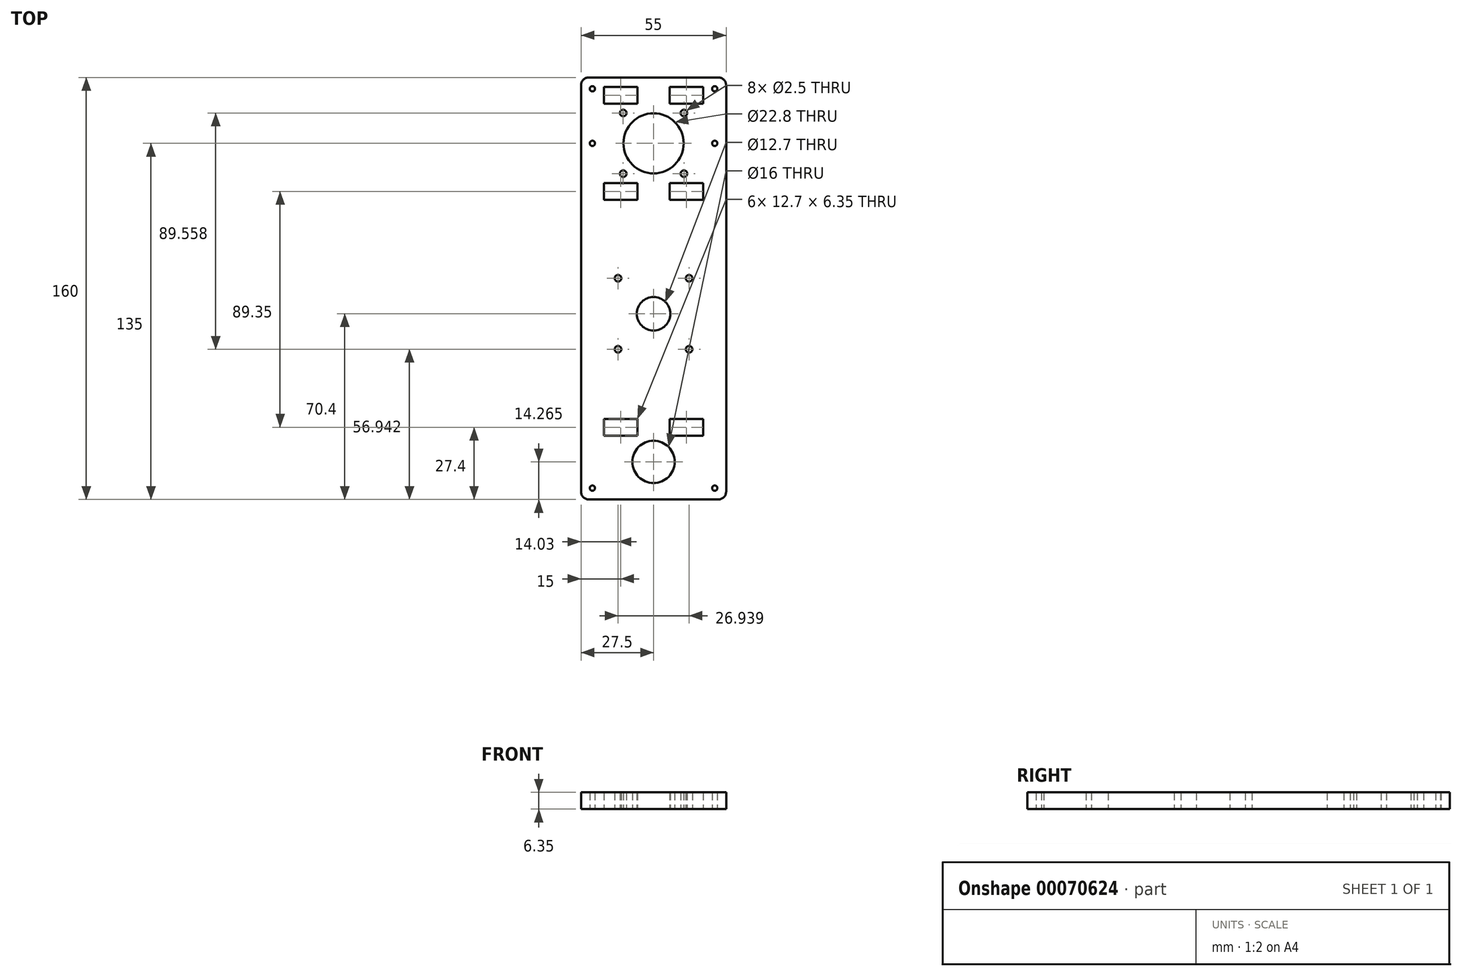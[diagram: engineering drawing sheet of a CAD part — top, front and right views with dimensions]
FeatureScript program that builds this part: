
annotation { "Feature Type Name" : "Feature", "Feature Type Description" : "" }
export const myFeature = defineFeature(function(context is Context, id is Id, definition is map)
    precondition{}
    {
        {
            var Q0;
            Q0=qCreatedBy(makeId("Top.planeOp"),FACE);
            var sketch = newSketch(context, id + "F0", { "sketchPlane" : qUnion([Q0])});
            skCircle(sketch, "E0", {"center": v(0, 0) * mm, "radius": 11.4 * mm});
            skLineSegment(sketch, "E1", {"start": v(0, 0) * mm, "end": v(0, 12.13) * mm});
            skLineSegment(sketch, "E2.bottom", {"start": v(-27.5, 25) * mm, "end": v(27.5, 25) * mm});
            skLineSegment(sketch, "E2.top", {"start": v(-27.5, -135) * mm, "end": v(27.5, -135) * mm});
            skLineSegment(sketch, "E2.left", {"start": v(-27.5, 25) * mm, "end": v(-27.5, -135) * mm});
            skLineSegment(sketch, "E2.right", {"start": v(27.5, 25) * mm, "end": v(27.5, -135) * mm});
            skPoint(sketch, "E3", {"position": v(-11.5, 11.5) * mm});
            skPoint(sketch, "E4.0.1.0", {"position": v(-11.5, -11.5) * mm});
            skPoint(sketch, "E4.1.0.0", {"position": v(11.5, 11.5) * mm});
            skPoint(sketch, "E4.1.1.0", {"position": v(11.5, -11.5) * mm});
            skLineSegment(sketch, "E4.direction1", {"start": v(-11.5, 11.5) * mm, "end": v(11.5, 11.5) * mm, "construction": true});
            skLineSegment(sketch, "E4.direction2", {"start": v(-11.5, 11.5) * mm, "end": v(-11.5, -11.5) * mm, "construction": true});
            skLineSegment(sketch, "E5.bottom", {"start": v(-18.85, 21.43) * mm, "end": v(-6.15, 21.43) * mm});
            skLineSegment(sketch, "E5.top", {"start": v(-18.85, 15.08) * mm, "end": v(-6.15, 15.08) * mm});
            skLineSegment(sketch, "E5.left", {"start": v(-18.85, 21.43) * mm, "end": v(-18.85, 15.07) * mm});
            skLineSegment(sketch, "E5.right", {"start": v(-6.15, 21.43) * mm, "end": v(-6.15, 15.07) * mm});
            skPoint(sketch, "E6", {"position": v(-12.5, 21.43) * mm});
            skLineSegment(sketch, "E7.0.1.0", {"start": v(-18.85, -21.43) * mm, "end": v(-6.15, -21.43) * mm});
            skLineSegment(sketch, "E7.0.1.1", {"start": v(-18.85, -15.07) * mm, "end": v(-6.15, -15.07) * mm});
            skLineSegment(sketch, "E7.0.1.2", {"start": v(-18.85, -15.07) * mm, "end": v(-18.85, -21.43) * mm});
            skLineSegment(sketch, "E7.0.1.3", {"start": v(-6.15, -15.07) * mm, "end": v(-6.15, -21.43) * mm});
            skPoint(sketch, "E7.0.1.4", {"position": v(-12.5, -15.07) * mm});
            skLineSegment(sketch, "E7.1.0.0", {"start": v(6.15, 15.08) * mm, "end": v(18.85, 15.08) * mm});
            skLineSegment(sketch, "E7.1.0.1", {"start": v(6.15, 21.43) * mm, "end": v(18.85, 21.43) * mm});
            skLineSegment(sketch, "E7.1.0.2", {"start": v(6.15, 21.43) * mm, "end": v(6.15, 15.07) * mm});
            skLineSegment(sketch, "E7.1.0.3", {"start": v(18.85, 21.43) * mm, "end": v(18.85, 15.07) * mm});
            skPoint(sketch, "E7.1.0.4", {"position": v(12.5, 21.43) * mm});
            skLineSegment(sketch, "E7.1.1.0", {"start": v(6.15, -21.43) * mm, "end": v(18.85, -21.43) * mm});
            skLineSegment(sketch, "E7.1.1.1", {"start": v(6.15, -15.07) * mm, "end": v(18.85, -15.07) * mm});
            skLineSegment(sketch, "E7.1.1.2", {"start": v(6.15, -15.07) * mm, "end": v(6.15, -21.43) * mm});
            skLineSegment(sketch, "E7.1.1.3", {"start": v(18.85, -15.07) * mm, "end": v(18.85, -21.43) * mm});
            skPoint(sketch, "E7.1.1.4", {"position": v(12.5, -15.07) * mm});
            skLineSegment(sketch, "E7.direction1", {"start": v(-18.85, 15.07) * mm, "end": v(6.15, 15.07) * mm, "construction": true});
            skLineSegment(sketch, "E7.direction2", {"start": v(-18.85, 15.07) * mm, "end": v(-18.85, -21.43) * mm, "construction": true});
            skPoint(sketch, "E8", {"position": v(0, -120.73) * mm});
            skPoint(sketch, "E9", {"position": v(-23.17, -130.67) * mm});
            skPoint(sketch, "E10", {"position": v(-23.17, 20.68) * mm});
            skPoint(sketch, "E11", {"position": v(-23.17, 0) * mm});
            skPoint(sketch, "E12.MirrorP", {"position": v(23.17, 20.68) * mm});
            skPoint(sketch, "E13.MirrorP", {"position": v(23.17, 0) * mm});
            skPoint(sketch, "E14.MirrorP", {"position": v(23.17, -130.67) * mm});
            skPoint(sketch, "E15", {"position": v(18.85, -18.25) * mm});
            skPoint(sketch, "E16", {"position": v(0, -64.6) * mm});
            skCircle(sketch, "E17", {"center": v(0, -64.6) * mm, "radius": 6.35 * mm});
            skPoint(sketch, "E18.3.0", {"position": v(-13.47, -51.13) * mm});
            skLineSegment(sketch, "E19", {"start": v(-13.42, -25) * mm, "end": v(-13.42, -25) * mm});
            skPoint(sketch, "E20.MirrorP", {"position": v(13.47, -51.13) * mm});
            skPoint(sketch, "E21.3.0", {"position": v(-13.47, -78.06) * mm});
            skPoint(sketch, "E22.MirrorP", {"position": v(13.47, -78.06) * mm});
            skLineSegment(sketch, "E23", {"start": v(0, -64.6) * mm, "end": v(56.6, -64.6) * mm, "construction": true});
            skCircle(sketch, "E24", {"center": v(0, -120.73) * mm, "radius": 8 * mm});
            skLineSegment(sketch, "E25.0.1.4", {"start": v(6.15, -104.42) * mm, "end": v(6.15, -110.77) * mm});
            skLineSegment(sketch, "E25.0.1.5", {"start": v(6.15, -104.42) * mm, "end": v(18.85, -104.42) * mm});
            skLineSegment(sketch, "E25.0.1.6", {"start": v(18.85, -104.42) * mm, "end": v(18.85, -110.77) * mm});
            skLineSegment(sketch, "E25.0.1.7", {"start": v(6.15, -110.77) * mm, "end": v(18.85, -110.77) * mm});
            skLineSegment(sketch, "E25.direction1", {"start": v(-18.85, -21.43) * mm, "end": v(-43.85, -21.43) * mm, "construction": true});
            skLineSegment(sketch, "E26.MirrorCS", {"start": v(-6.15, -104.42) * mm, "end": v(-6.15, -110.77) * mm});
            skLineSegment(sketch, "E27.MirrorCS", {"start": v(-18.85, -104.42) * mm, "end": v(-18.85, -110.77) * mm});
            skLineSegment(sketch, "E28.MirrorCS", {"start": v(-6.15, -110.77) * mm, "end": v(-18.85, -110.77) * mm});
            skLineSegment(sketch, "E29.MirrorCS", {"start": v(-6.15, -104.42) * mm, "end": v(-18.85, -104.42) * mm});
            skSolve(sketch);
        }
        {
            var Q0;
            Q0=makeQuery(id+"F0.imprint","IMPRINT",FACE,{"disambiguationData":[TD([[makeQuery(id+"F0.imprint","IMPRINT",EDGE,{"derivedFrom":sQuery(id+"F0.wireOp",EDGE,"E0")}),-1.0]])]});
            extrude(context, id + "F1", {"entities" : qUnion([Q0]), "depth" : 6.35 * mm});
        }
        {
            var Q0;
            Q0=sQuery(id+"F0.wireOp",VERTEX,"E3");
            var Q1;
            Q1=sQuery(id+"F0.wireOp",VERTEX,"E4.1.0.0");
            var Q2;
            Q2=sQuery(id+"F0.wireOp",VERTEX,"E4.1.1.0");
            var Q3;
            Q3=sQuery(id+"F0.wireOp",VERTEX,"E4.0.1.0");
            var Q4;
            Q4=sQuery(id+"F0.wireOp",VERTEX,"E18.3.0");
            var Q5;
            Q5=sQuery(id+"F0.wireOp",VERTEX,"E20.MirrorP");
            var Q6;
            Q6=sQuery(id+"F0.wireOp",VERTEX,"E22.MirrorP");
            var Q7;
            Q7=sQuery(id+"F0.wireOp",VERTEX,"E21.3.0");
            var Q8;
            Q8=makeQuery(id+"F1.opExtrude","SWEPT_BODY",BODY,{"disambiguationData":[OSD([sQuery(id+"F0.wireOp",EDGE,"E0"),sQuery(id+"F0.wireOp",EDGE,"E2.bottom"),sQuery(id+"F0.wireOp",EDGE,"E2.top"),sQuery(id+"F0.wireOp",EDGE,"E2.left"),sQuery(id+"F0.wireOp",EDGE,"E2.right")])]});
            hole(context, id + "F2", {"style" : HoleStyle.SIMPLE, "endStyle" : HoleEndStyle.THROUGH, "oppositeDirection" : true, "holeDiameter" : 2.5 * mm, "locations" : qUnion([Q0, Q1, Q2, Q3, Q4, Q5, Q6, Q7]), "scope" : qUnion([Q8]), "isTappedThrough" : true});
        }
        {
            var Q0;
            Q0=makeQuery(id+"F1.opExtrude","SWEPT_EDGE",EDGE,{"disambiguationData":[OSD([sQuery(id+"F0.wireOp",EDGE,"E2.top"),sQuery(id+"F0.wireOp",EDGE,"E2.left")])]});
            var Q1;
            Q1=makeQuery(id+"F1.opExtrude","SWEPT_EDGE",EDGE,{"disambiguationData":[OSD([sQuery(id+"F0.wireOp",EDGE,"E2.top"),sQuery(id+"F0.wireOp",EDGE,"E2.right")])]});
            var Q2;
            Q2=makeQuery(id+"F1.opExtrude","SWEPT_EDGE",EDGE,{"disambiguationData":[OSD([sQuery(id+"F0.wireOp",EDGE,"E2.bottom"),sQuery(id+"F0.wireOp",EDGE,"E2.right")])]});
            var Q3;
            Q3=makeQuery(id+"F1.opExtrude","SWEPT_EDGE",EDGE,{"disambiguationData":[OSD([sQuery(id+"F0.wireOp",EDGE,"E2.bottom"),sQuery(id+"F0.wireOp",EDGE,"E2.left")])]});
            fillet(context, id + "F3", {"entities" : qUnion([Q0, Q1, Q2, Q3]), "radius" : 3 * mm, "tangentPropagation" : true, "allowEdgeOverflow" : false});
        }
        {
            var Q0;
            Q0=sQuery(id+"F0.wireOp",VERTEX,"E9");
            var Q1;
            Q1=sQuery(id+"F0.wireOp",VERTEX,"E14.MirrorP");
            var Q2;
            Q2=sQuery(id+"F0.wireOp",VERTEX,"E13.MirrorP");
            var Q3;
            Q3=sQuery(id+"F0.wireOp",VERTEX,"E12.MirrorP");
            var Q4;
            Q4=sQuery(id+"F0.wireOp",VERTEX,"E10");
            var Q5;
            Q5=sQuery(id+"F0.wireOp",VERTEX,"E11");
            var Q6;
            Q6=makeQuery(id+"F1.opExtrude","SWEPT_BODY",BODY,{"disambiguationData":[OSD([sQuery(id+"F0.wireOp",EDGE,"E0"),sQuery(id+"F0.wireOp",EDGE,"E2.bottom"),sQuery(id+"F0.wireOp",EDGE,"E2.top"),sQuery(id+"F0.wireOp",EDGE,"E2.left"),sQuery(id+"F0.wireOp",EDGE,"E2.right"),sQuery(id+"F0.wireOp",EDGE,"E5.bottom"),sQuery(id+"F0.wireOp",EDGE,"E5.top"),sQuery(id+"F0.wireOp",EDGE,"E5.left"),sQuery(id+"F0.wireOp",EDGE,"E5.right"),sQuery(id+"F0.wireOp",EDGE,"E7.0.1.0"),sQuery(id+"F0.wireOp",EDGE,"E7.0.1.1"),sQuery(id+"F0.wireOp",EDGE,"E7.0.1.2"),sQuery(id+"F0.wireOp",EDGE,"E7.0.1.3"),sQuery(id+"F0.wireOp",EDGE,"E7.1.0.0"),sQuery(id+"F0.wireOp",EDGE,"E7.1.0.1"),sQuery(id+"F0.wireOp",EDGE,"E7.1.0.2"),sQuery(id+"F0.wireOp",EDGE,"E7.1.0.3"),sQuery(id+"F0.wireOp",EDGE,"E7.1.1.0"),sQuery(id+"F0.wireOp",EDGE,"E7.1.1.1"),sQuery(id+"F0.wireOp",EDGE,"E7.1.1.2"),sQuery(id+"F0.wireOp",EDGE,"E7.1.1.3")])]});
            hole(context, id + "F4", {"style" : HoleStyle.SIMPLE, "endStyle" : HoleEndStyle.THROUGH, "oppositeDirection" : true, "holeDiameter" : 2 * mm, "locations" : qUnion([Q0, Q1, Q2, Q3, Q4, Q5]), "scope" : qUnion([Q6]), "isTappedThrough" : true});
        }
    });
